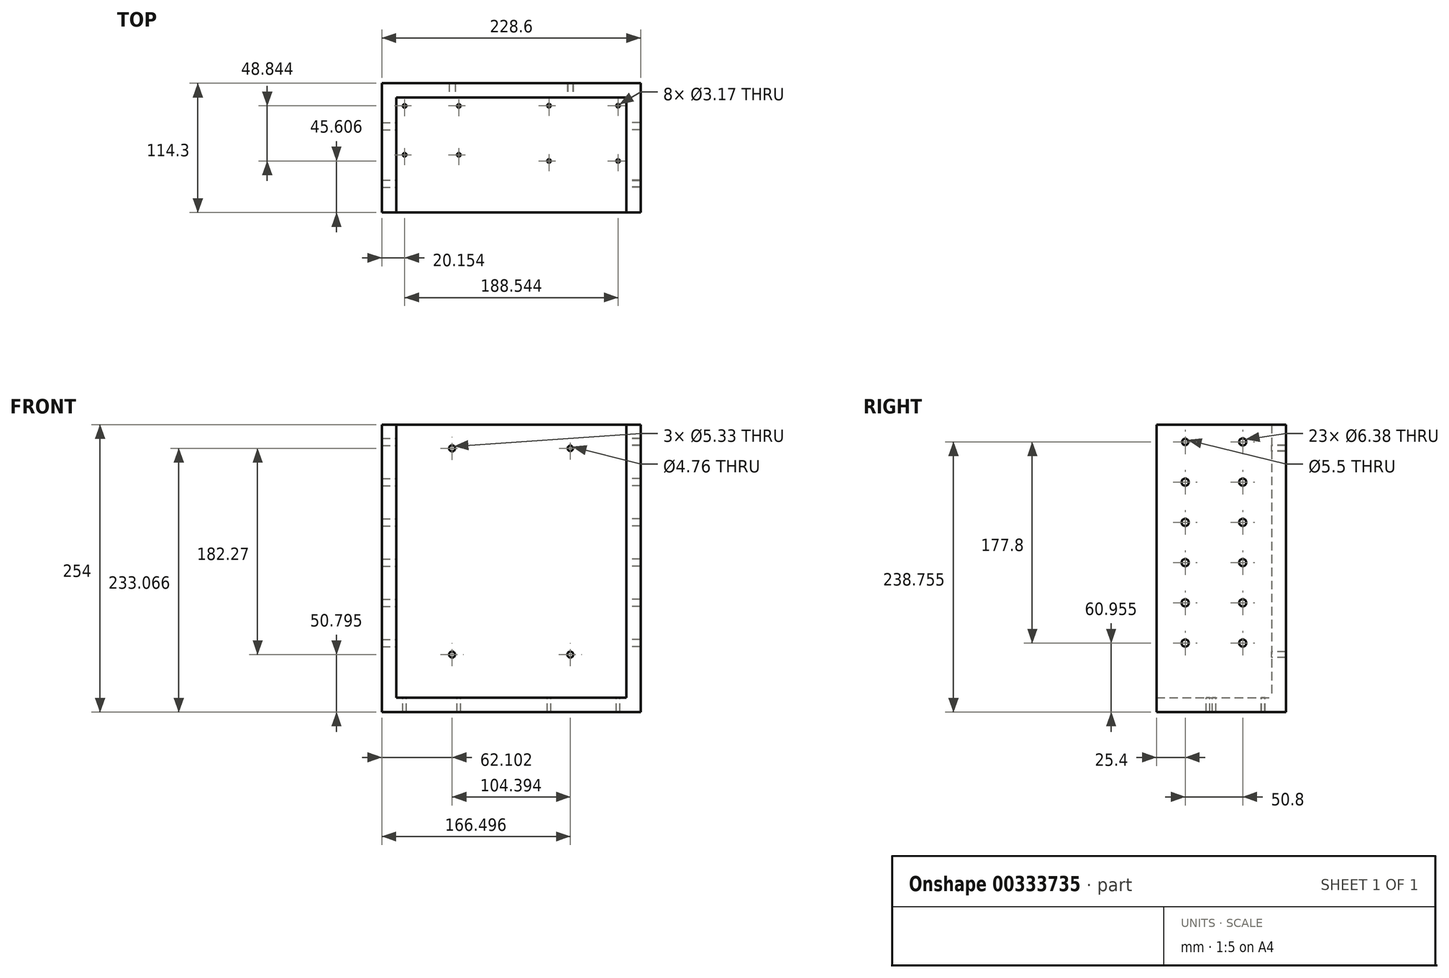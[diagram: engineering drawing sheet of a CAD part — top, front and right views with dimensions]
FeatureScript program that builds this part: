
annotation { "Feature Type Name" : "Feature", "Feature Type Description" : "" }
export const myFeature = defineFeature(function(context is Context, id is Id, definition is map)
    precondition{}
    {
        {
            var Q0;
            Q0=qCreatedBy(makeId("Front.planeOp"),FACE);
            var sketch = newSketch(context, id + "F0", { "sketchPlane" : qUnion([Q0])});
            skLineSegment(sketch, "E0.bottom", {"start": v(-108.75, 153.38) * mm, "end": v(119.85, 153.38) * mm});
            skLineSegment(sketch, "E0.top", {"start": v(-108.75, -100.62) * mm, "end": v(119.85, -100.62) * mm});
            skLineSegment(sketch, "E0.left", {"start": v(-108.75, 153.38) * mm, "end": v(-108.75, -100.62) * mm});
            skLineSegment(sketch, "E0.right", {"start": v(119.85, 153.38) * mm, "end": v(119.85, -100.62) * mm});
            skSolve(sketch);
        }
        {
            var Q0;
            Q0=makeQuery(id+"F0.imprint","IMPRINT",FACE,{"disambiguationData":[TD([[makeQuery(id+"F0.imprint","IMPRINT",EDGE,{"derivedFrom":sQuery(id+"F0.wireOp",EDGE,"E0.bottom")}),-1.0]])]});
            extrude(context, id + "F1", {"entities" : qUnion([Q0]), "depth" : 12.7 * mm});
        }
        {
            var Q0;
            Q0=makeQuery(id+"F1.opExtrude","CAP_FACE",FACE,{"disambiguationData":[OSD([sQuery(id+"F0.wireOp",EDGE,"E0.bottom"),sQuery(id+"F0.wireOp",EDGE,"E0.top"),sQuery(id+"F0.wireOp",EDGE,"E0.left"),sQuery(id+"F0.wireOp",EDGE,"E0.right")])],"isStart":false});
            var sketch = newSketch(context, id + "F2", { "sketchPlane" : qUnion([Q0])});
            skLineSegment(sketch, "E1", {"start": v(-108.75, 153.38) * mm, "end": v(-96.05, 153.38) * mm});
            skLineSegment(sketch, "E2", {"start": v(-96.05, 153.38) * mm, "end": v(-96.05, -87.92) * mm});
            skLineSegment(sketch, "E3", {"start": v(-96.05, -87.92) * mm, "end": v(107.15, -87.92) * mm});
            skLineSegment(sketch, "E4", {"start": v(107.15, -87.92) * mm, "end": v(107.15, 153.38) * mm});
            skLineSegment(sketch, "E5", {"start": v(107.15, 153.38) * mm, "end": v(119.85, 153.38) * mm});
            skLineSegment(sketch, "E6", {"start": v(119.85, 153.38) * mm, "end": v(119.85, -100.62) * mm});
            skLineSegment(sketch, "E7", {"start": v(119.85, -100.62) * mm, "end": v(-108.75, -100.62) * mm});
            skLineSegment(sketch, "E8", {"start": v(-108.75, -100.62) * mm, "end": v(-108.75, 153.38) * mm});
            skSolve(sketch);
        }
        {
            var Q0;
            Q0=makeQuery(id+"F2.imprint","IMPRINT",FACE,{"disambiguationData":[TD([[makeQuery(id+"F2.imprint","IMPRINT",EDGE,{"derivedFrom":sQuery(id+"F2.wireOp",EDGE,"E1")}),-1.0]])]});
            extrude(context, id + "F3", {"entities" : qUnion([Q0]), "operationType" : NewBodyOperationType.ADD, "depth" : 101.6 * mm});
        }
        {
            var Q0;
            Q0=makeQuery(id+"F1.opExtrude","CAP_FACE",FACE,{"disambiguationData":[OSD([sQuery(id+"F0.wireOp",EDGE,"E0.bottom"),sQuery(id+"F0.wireOp",EDGE,"E0.top"),sQuery(id+"F0.wireOp",EDGE,"E0.left"),sQuery(id+"F0.wireOp",EDGE,"E0.right")])],"isStart":false});
            var sketch = newSketch(context, id + "F4", { "sketchPlane" : qUnion([Q0])});
            skCircle(sketch, "E9", {"center": v(-46.65, 132.45) * mm, "radius": 2.67 * mm});
            skCircle(sketch, "E10", {"center": v(57.75, 132.45) * mm, "radius": 2.38 * mm});
            skCircle(sketch, "E11", {"center": v(-46.65, -49.82) * mm, "radius": 2.67 * mm});
            skCircle(sketch, "E12", {"center": v(57.75, -49.82) * mm, "radius": 2.67 * mm});
            skLineSegment(sketch, "E13", {"start": v(-46.65, 132.45) * mm, "end": v(-46.65, -49.82) * mm, "construction": true});
            skLineSegment(sketch, "E14", {"start": v(57.75, 132.45) * mm, "end": v(107.15, 132.45) * mm, "construction": true});
            skLineSegment(sketch, "E15", {"start": v(-46.65, 132.45) * mm, "end": v(-96.05, 132.45) * mm, "construction": true});
            skSolve(sketch);
        }
        {
            var Q0;
            Q0=makeQuery(id+"F4.imprint","IMPRINT",FACE,{"disambiguationData":[TD([[makeQuery(id+"F4.imprint","IMPRINT",EDGE,{"derivedFrom":sQuery(id+"F4.wireOp",EDGE,"E9")}),1.0]])]});
            var Q1;
            Q1=makeQuery(id+"F4.imprint","IMPRINT",FACE,{"disambiguationData":[TD([[makeQuery(id+"F4.imprint","IMPRINT",EDGE,{"derivedFrom":sQuery(id+"F4.wireOp",EDGE,"E10")}),1.0]])]});
            var Q2;
            Q2=makeQuery(id+"F4.imprint","IMPRINT",FACE,{"disambiguationData":[TD([[makeQuery(id+"F4.imprint","IMPRINT",EDGE,{"derivedFrom":sQuery(id+"F4.wireOp",EDGE,"E12")}),1.0]])]});
            var Q3;
            Q3=makeQuery(id+"F4.imprint","IMPRINT",FACE,{"disambiguationData":[TD([[makeQuery(id+"F4.imprint","IMPRINT",EDGE,{"derivedFrom":sQuery(id+"F4.wireOp",EDGE,"E11")}),1.0]])]});
            extrude(context, id + "F5", {"entities" : qUnion([Q0, Q1, Q2, Q3]), "operationType" : NewBodyOperationType.REMOVE, "oppositeDirection" : true, "depth" : 25.4 * mm});
        }
        {
            var Q0;
            Q0=makeQuery(id+"F3.opExtrude","SWEPT_FACE",FACE,{"disambiguationData":[OSD([sQuery(id+"F2.wireOp",EDGE,"E4")])]});
            var sketch = newSketch(context, id + "F6", { "sketchPlane" : qUnion([Q0])});
            skCircle(sketch, "E16", {"center": v(38.1, 138.14) * mm, "radius": 3.19 * mm});
            skCircle(sketch, "E17", {"center": v(88.9, 138.14) * mm, "radius": 2.75 * mm});
            skCircle(sketch, "E18.0.1.0", {"center": v(38.1, 102.58) * mm, "radius": 3.19 * mm});
            skCircle(sketch, "E18.0.2.0", {"center": v(38.1, 67.02) * mm, "radius": 3.19 * mm});
            skCircle(sketch, "E18.0.3.0", {"center": v(38.1, 31.46) * mm, "radius": 3.19 * mm});
            skCircle(sketch, "E18.0.4.0", {"center": v(38.1, -4.1) * mm, "radius": 3.19 * mm});
            skCircle(sketch, "E18.0.5.0", {"center": v(38.1, -39.66) * mm, "radius": 3.19 * mm});
            skCircle(sketch, "E18.1.0.0", {"center": v(88.9, 138.14) * mm, "radius": 3.19 * mm});
            skCircle(sketch, "E18.1.1.0", {"center": v(88.9, 102.58) * mm, "radius": 3.19 * mm});
            skCircle(sketch, "E18.1.2.0", {"center": v(88.9, 67.02) * mm, "radius": 3.19 * mm});
            skCircle(sketch, "E18.1.3.0", {"center": v(88.9, 31.46) * mm, "radius": 3.19 * mm});
            skCircle(sketch, "E18.1.4.0", {"center": v(88.9, -4.1) * mm, "radius": 3.19 * mm});
            skCircle(sketch, "E18.1.5.0", {"center": v(88.9, -39.66) * mm, "radius": 3.19 * mm});
            skLineSegment(sketch, "E18.direction1", {"start": v(38.1, 138.14) * mm, "end": v(88.9, 138.14) * mm, "construction": true});
            skLineSegment(sketch, "E18.direction2", {"start": v(38.1, 138.14) * mm, "end": v(38.1, 102.58) * mm, "construction": true});
            skSolve(sketch);
        }
        {
            var Q0;
            Q0=makeQuery(id+"F3.opExtrude","SWEPT_FACE",FACE,{"disambiguationData":[OSD([sQuery(id+"F2.wireOp",EDGE,"E2")])]});
            var sketch = newSketch(context, id + "F7", { "sketchPlane" : qUnion([Q0])});
            skCircle(sketch, "E19", {"center": v(-88.9, 138.14) * mm, "radius": 3.19 * mm});
            skCircle(sketch, "E20.0.1.0", {"center": v(-88.9, 102.58) * mm, "radius": 3.19 * mm});
            skCircle(sketch, "E20.0.2.0", {"center": v(-88.9, 67.02) * mm, "radius": 3.19 * mm});
            skCircle(sketch, "E20.0.3.0", {"center": v(-88.9, 31.46) * mm, "radius": 3.19 * mm});
            skCircle(sketch, "E20.0.4.0", {"center": v(-88.9, -4.1) * mm, "radius": 3.19 * mm});
            skCircle(sketch, "E20.0.5.0", {"center": v(-88.9, -39.66) * mm, "radius": 3.19 * mm});
            skCircle(sketch, "E20.1.0.0", {"center": v(-38.1, 138.14) * mm, "radius": 3.19 * mm});
            skCircle(sketch, "E20.1.1.0", {"center": v(-38.1, 102.58) * mm, "radius": 3.19 * mm});
            skCircle(sketch, "E20.1.2.0", {"center": v(-38.1, 67.02) * mm, "radius": 3.19 * mm});
            skCircle(sketch, "E20.1.3.0", {"center": v(-38.1, 31.46) * mm, "radius": 3.19 * mm});
            skCircle(sketch, "E20.1.4.0", {"center": v(-38.1, -4.1) * mm, "radius": 3.19 * mm});
            skCircle(sketch, "E20.1.5.0", {"center": v(-38.1, -39.66) * mm, "radius": 3.19 * mm});
            skLineSegment(sketch, "E20.direction1", {"start": v(-88.9, 138.14) * mm, "end": v(-38.1, 138.14) * mm, "construction": true});
            skLineSegment(sketch, "E20.direction2", {"start": v(-88.9, 138.14) * mm, "end": v(-88.9, 102.58) * mm, "construction": true});
            skSolve(sketch);
        }
        {
            var Q0;
            Q0=makeQuery(id+"F7.imprint","IMPRINT",FACE,{"disambiguationData":[TD([[makeQuery(id+"F7.imprint","IMPRINT",EDGE,{"derivedFrom":sQuery(id+"F7.wireOp",EDGE,"E20.0.1.0")}),1.0]])]});
            var Q1;
            Q1=makeQuery(id+"F7.imprint","IMPRINT",FACE,{"disambiguationData":[TD([[makeQuery(id+"F7.imprint","IMPRINT",EDGE,{"derivedFrom":sQuery(id+"F7.wireOp",EDGE,"E19")}),1.0]])]});
            var Q2;
            Q2=makeQuery(id+"F7.imprint","IMPRINT",FACE,{"disambiguationData":[TD([[makeQuery(id+"F7.imprint","IMPRINT",EDGE,{"derivedFrom":sQuery(id+"F7.wireOp",EDGE,"E20.1.0.0")}),1.0]])]});
            var Q3;
            Q3=makeQuery(id+"F7.imprint","IMPRINT",FACE,{"disambiguationData":[TD([[makeQuery(id+"F7.imprint","IMPRINT",EDGE,{"derivedFrom":sQuery(id+"F7.wireOp",EDGE,"E20.1.1.0")}),1.0]])]});
            var Q4;
            Q4=makeQuery(id+"F7.imprint","IMPRINT",FACE,{"disambiguationData":[TD([[makeQuery(id+"F7.imprint","IMPRINT",EDGE,{"derivedFrom":sQuery(id+"F7.wireOp",EDGE,"E20.1.2.0")}),1.0]])]});
            var Q5;
            Q5=makeQuery(id+"F7.imprint","IMPRINT",FACE,{"disambiguationData":[TD([[makeQuery(id+"F7.imprint","IMPRINT",EDGE,{"derivedFrom":sQuery(id+"F7.wireOp",EDGE,"E20.0.2.0")}),1.0]])]});
            var Q6;
            Q6=makeQuery(id+"F7.imprint","IMPRINT",FACE,{"disambiguationData":[TD([[makeQuery(id+"F7.imprint","IMPRINT",EDGE,{"derivedFrom":sQuery(id+"F7.wireOp",EDGE,"E20.1.3.0")}),1.0]])]});
            var Q7;
            Q7=makeQuery(id+"F7.imprint","IMPRINT",FACE,{"disambiguationData":[TD([[makeQuery(id+"F7.imprint","IMPRINT",EDGE,{"derivedFrom":sQuery(id+"F7.wireOp",EDGE,"E20.0.3.0")}),1.0]])]});
            var Q8;
            Q8=makeQuery(id+"F7.imprint","IMPRINT",FACE,{"disambiguationData":[TD([[makeQuery(id+"F7.imprint","IMPRINT",EDGE,{"derivedFrom":sQuery(id+"F7.wireOp",EDGE,"E20.0.5.0")}),1.0]])]});
            var Q9;
            Q9=makeQuery(id+"F7.imprint","IMPRINT",FACE,{"disambiguationData":[TD([[makeQuery(id+"F7.imprint","IMPRINT",EDGE,{"derivedFrom":sQuery(id+"F7.wireOp",EDGE,"E20.0.4.0")}),1.0]])]});
            var Q10;
            Q10=makeQuery(id+"F7.imprint","IMPRINT",FACE,{"disambiguationData":[TD([[makeQuery(id+"F7.imprint","IMPRINT",EDGE,{"derivedFrom":sQuery(id+"F7.wireOp",EDGE,"E20.1.4.0")}),1.0]])]});
            var Q11;
            Q11=makeQuery(id+"F7.imprint","IMPRINT",FACE,{"disambiguationData":[TD([[makeQuery(id+"F7.imprint","IMPRINT",EDGE,{"derivedFrom":sQuery(id+"F7.wireOp",EDGE,"E20.1.5.0")}),1.0]])]});
            extrude(context, id + "F8", {"entities" : qUnion([Q0, Q1, Q2, Q3, Q4, Q5, Q6, Q7, Q8, Q9, Q10, Q11]), "operationType" : NewBodyOperationType.REMOVE, "oppositeDirection" : true, "depth" : 25.4 * mm});
        }
        {
            var Q0;
            Q0=makeQuery(id+"F6.imprint","IMPRINT",FACE,{"disambiguationData":[TD([[makeQuery(id+"F6.imprint","IMPRINT",EDGE,{"derivedFrom":sQuery(id+"F6.wireOp",EDGE,"E16")}),1.0]])]});
            var Q1;
            Q1=makeQuery(id+"F6.imprint","IMPRINT",FACE,{"disambiguationData":[TD([[makeQuery(id+"F6.imprint","IMPRINT",EDGE,{"derivedFrom":sQuery(id+"F6.wireOp",EDGE,"E17")}),1.0]])]});
            var Q2;
            Q2=makeQuery(id+"F6.imprint","IMPRINT",FACE,{"disambiguationData":[TD([[makeQuery(id+"F6.imprint","IMPRINT",EDGE,{"derivedFrom":sQuery(id+"F6.wireOp",EDGE,"E18.0.1.0")}),1.0]])]});
            var Q3;
            Q3=makeQuery(id+"F6.imprint","IMPRINT",FACE,{"disambiguationData":[TD([[makeQuery(id+"F6.imprint","IMPRINT",EDGE,{"derivedFrom":sQuery(id+"F6.wireOp",EDGE,"E18.1.1.0")}),1.0]])]});
            var Q4;
            Q4=makeQuery(id+"F6.imprint","IMPRINT",FACE,{"disambiguationData":[TD([[makeQuery(id+"F6.imprint","IMPRINT",EDGE,{"derivedFrom":sQuery(id+"F6.wireOp",EDGE,"E18.0.2.0")}),1.0]])]});
            var Q5;
            Q5=makeQuery(id+"F6.imprint","IMPRINT",FACE,{"disambiguationData":[TD([[makeQuery(id+"F6.imprint","IMPRINT",EDGE,{"derivedFrom":sQuery(id+"F6.wireOp",EDGE,"E18.1.2.0")}),1.0]])]});
            var Q6;
            Q6=makeQuery(id+"F6.imprint","IMPRINT",FACE,{"disambiguationData":[TD([[makeQuery(id+"F6.imprint","IMPRINT",EDGE,{"derivedFrom":sQuery(id+"F6.wireOp",EDGE,"E18.0.3.0")}),1.0]])]});
            var Q7;
            Q7=makeQuery(id+"F6.imprint","IMPRINT",FACE,{"disambiguationData":[TD([[makeQuery(id+"F6.imprint","IMPRINT",EDGE,{"derivedFrom":sQuery(id+"F6.wireOp",EDGE,"E18.1.3.0")}),1.0]])]});
            var Q8;
            Q8=makeQuery(id+"F6.imprint","IMPRINT",FACE,{"disambiguationData":[TD([[makeQuery(id+"F6.imprint","IMPRINT",EDGE,{"derivedFrom":sQuery(id+"F6.wireOp",EDGE,"E18.0.4.0")}),1.0]])]});
            var Q9;
            Q9=makeQuery(id+"F6.imprint","IMPRINT",FACE,{"disambiguationData":[TD([[makeQuery(id+"F6.imprint","IMPRINT",EDGE,{"derivedFrom":sQuery(id+"F6.wireOp",EDGE,"E18.1.4.0")}),1.0]])]});
            var Q10;
            Q10=makeQuery(id+"F6.imprint","IMPRINT",FACE,{"disambiguationData":[TD([[makeQuery(id+"F6.imprint","IMPRINT",EDGE,{"derivedFrom":sQuery(id+"F6.wireOp",EDGE,"E18.0.5.0")}),1.0]])]});
            var Q11;
            Q11=makeQuery(id+"F6.imprint","IMPRINT",FACE,{"disambiguationData":[TD([[makeQuery(id+"F6.imprint","IMPRINT",EDGE,{"derivedFrom":sQuery(id+"F6.wireOp",EDGE,"E18.1.5.0")}),1.0]])]});
            extrude(context, id + "F9", {"entities" : qUnion([Q0, Q1, Q2, Q3, Q4, Q5, Q6, Q7, Q8, Q9, Q10, Q11]), "operationType" : NewBodyOperationType.REMOVE, "oppositeDirection" : true, "depth" : 25.4 * mm});
        }
        {
            var Q0;
            Q0=makeQuery(id+"F3.opExtrude","SWEPT_FACE",FACE,{"disambiguationData":[OSD([sQuery(id+"F2.wireOp",EDGE,"E3")])]});
            var sketch = newSketch(context, id + "F10", { "sketchPlane" : qUnion([Q0])});
            skLineSegment(sketch, "E21.bottom", {"start": v(-92.88, -15.88) * mm, "end": v(-36.49, -15.88) * mm, "construction": true});
            skLineSegment(sketch, "E21.top", {"start": v(-92.88, -67.44) * mm, "end": v(-36.49, -67.44) * mm, "construction": true});
            skLineSegment(sketch, "E21.left", {"start": v(-92.88, -15.88) * mm, "end": v(-92.88, -67.44) * mm, "construction": true});
            skLineSegment(sketch, "E21.right", {"start": v(-36.49, -15.88) * mm, "end": v(-36.49, -67.44) * mm, "construction": true});
            skLineSegment(sketch, "E22.bottom", {"start": v(103.97, -15.87) * mm, "end": v(34.89, -15.88) * mm, "construction": true});
            skLineSegment(sketch, "E22.top", {"start": v(103.97, -72.67) * mm, "end": v(34.89, -72.67) * mm, "construction": true});
            skLineSegment(sketch, "E22.left", {"start": v(103.97, -15.87) * mm, "end": v(103.97, -72.67) * mm, "construction": true});
            skLineSegment(sketch, "E22.right", {"start": v(34.89, -15.88) * mm, "end": v(34.89, -72.67) * mm, "construction": true});
            skLineSegment(sketch, "E23", {"start": v(-36.49, -41.66) * mm, "end": v(-92.88, -41.66) * mm, "construction": true});
            skLineSegment(sketch, "E24", {"start": v(-64.68, -67.44) * mm, "end": v(-64.68, -15.88) * mm, "construction": true});
            skLineSegment(sketch, "E25", {"start": v(69.43, -72.67) * mm, "end": v(69.43, -15.88) * mm, "construction": true});
            skLineSegment(sketch, "E26", {"start": v(34.89, -44.27) * mm, "end": v(103.97, -44.27) * mm, "construction": true});
            skPoint(sketch, "E27", {"position": v(69.43, -44.27) * mm});
            skPoint(sketch, "E28", {"position": v(-64.68, -41.66) * mm});
            skLineSegment(sketch, "E29.bottom", {"start": v(-40.77, -63.27) * mm, "end": v(-88.6, -63.27) * mm, "construction": true});
            skLineSegment(sketch, "E29.top", {"start": v(-40.77, -20.04) * mm, "end": v(-88.6, -20.04) * mm, "construction": true});
            skLineSegment(sketch, "E29.left", {"start": v(-40.77, -63.27) * mm, "end": v(-40.77, -20.04) * mm, "construction": true});
            skLineSegment(sketch, "E29.right", {"start": v(-88.6, -63.27) * mm, "end": v(-88.6, -20.04) * mm, "construction": true});
            skLineSegment(sketch, "E30.bottom", {"start": v(99.95, -68.7) * mm, "end": v(38.91, -68.7) * mm, "construction": true});
            skLineSegment(sketch, "E30.top", {"start": v(99.95, -19.85) * mm, "end": v(38.91, -19.85) * mm, "construction": true});
            skLineSegment(sketch, "E30.left", {"start": v(99.95, -68.7) * mm, "end": v(99.95, -19.85) * mm, "construction": true});
            skLineSegment(sketch, "E30.right", {"start": v(38.91, -68.7) * mm, "end": v(38.91, -19.85) * mm, "construction": true});
            skCircle(sketch, "E31", {"center": v(38.91, -19.85) * mm, "radius": 1.59 * mm});
            skCircle(sketch, "E32", {"center": v(99.95, -19.85) * mm, "radius": 1.59 * mm});
            skCircle(sketch, "E33", {"center": v(99.95, -68.7) * mm, "radius": 1.59 * mm});
            skCircle(sketch, "E34", {"center": v(38.91, -68.7) * mm, "radius": 1.59 * mm});
            skCircle(sketch, "E35", {"center": v(-40.77, -20.04) * mm, "radius": 1.59 * mm});
            skCircle(sketch, "E36", {"center": v(-40.77, -63.27) * mm, "radius": 1.59 * mm});
            skCircle(sketch, "E37", {"center": v(-88.6, -63.27) * mm, "radius": 1.59 * mm});
            skCircle(sketch, "E38", {"center": v(-88.6, -20.04) * mm, "radius": 1.59 * mm});
            skSolve(sketch);
        }
        {
            var Q0;
            Q0 = qSketchRegion(id + "F10", true);
            extrude(context, id + "F11", {"entities" : qUnion([Q0]), "operationType" : NewBodyOperationType.REMOVE, "endBound" : BoundingType.THROUGH_ALL, "oppositeDirection" : true, "depth" : 25.4 * mm});
        }
    });
